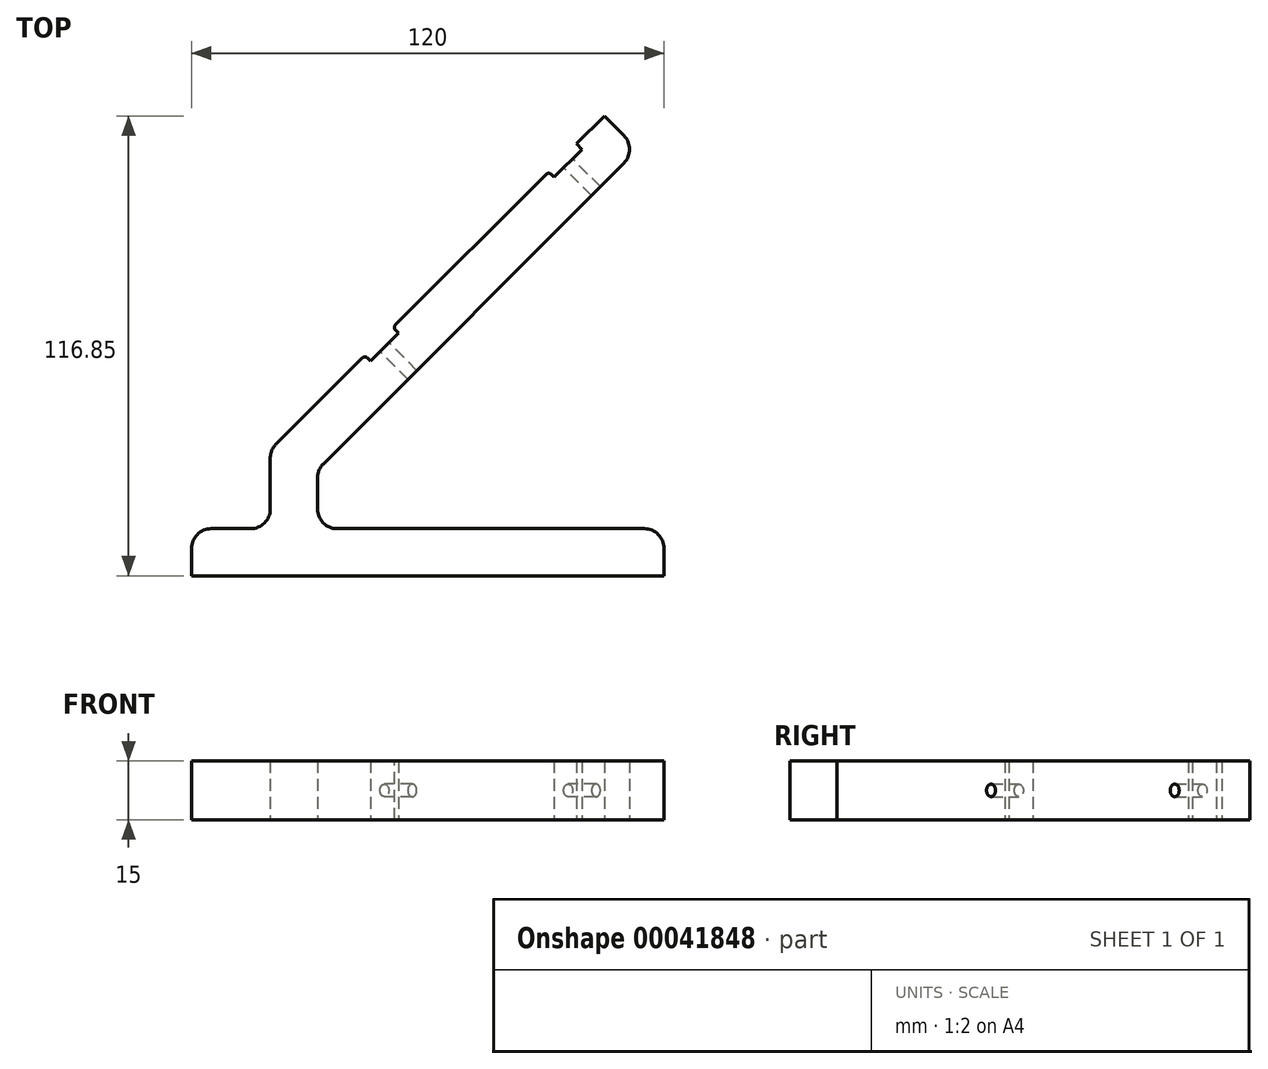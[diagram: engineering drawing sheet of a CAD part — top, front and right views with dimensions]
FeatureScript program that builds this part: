
annotation { "Feature Type Name" : "Feature", "Feature Type Description" : "" }
export const myFeature = defineFeature(function(context is Context, id is Id, definition is map)
    precondition{}
    {
        {
            var Q0;
            Q0=qCreatedBy(makeId("Top.planeOp"),FACE);
            var sketch = newSketch(context, id + "F0", { "sketchPlane" : qUnion([Q0])});
            skLineSegment(sketch, "E0.bottom", {"start": v(60, -6) * mm, "end": v(-60, -6) * mm});
            skLineSegment(sketch, "E0.top", {"start": v(60, 6) * mm, "end": v(-60, 6) * mm});
            skLineSegment(sketch, "E0.left", {"start": v(60, -6) * mm, "end": v(60, 6) * mm});
            skLineSegment(sketch, "E0.right", {"start": v(-60, -6) * mm, "end": v(-60, 6) * mm});
            skPoint(sketch, "E0.middle", {"position": v(0, 0) * mm});
            skLineSegment(sketch, "E1", {"start": v(-40, 26) * mm, "end": v(44.85, 110.85) * mm});
            skLineSegment(sketch, "E2", {"start": v(44.85, 110.85) * mm, "end": v(53.34, 102.37) * mm});
            skLineSegment(sketch, "E3", {"start": v(53.34, 102.37) * mm, "end": v(-28, 21.03) * mm});
            skLineSegment(sketch, "E4", {"start": v(-40, 26) * mm, "end": v(-40, 6) * mm});
            skLineSegment(sketch, "E5", {"start": v(-28, 21.03) * mm, "end": v(-28, 6) * mm});
            skSolve(sketch);
        }
        {
            var Q0;
            {var subQ0=sQuery(id+"F0.wireOp",EDGE,"E1");Q0=makeQuery(id+"F0.imprint","IMPRINT",FACE,{"disambiguationData":[TD([[makeQuery(id+"F0.imprint","IMPRINT",EDGE,{"derivedFrom":subQ0}),-1.0]])]});}
            var Q1;
            Q1=makeQuery(id+"F0.imprint","IMPRINT",FACE,{"disambiguationData":[TD([[makeQuery(id+"F0.imprint","IMPRINT",EDGE,{"derivedFrom":sQuery(id+"F0.wireOp",EDGE,"E0.bottom")}),-1.0]])]});
            extrude(context, id + "F1", {"entities" : qUnion([Q0, Q1]), "depth" : 15 * mm});
        }
        {
            var Q0;
            Q0=makeQuery(id+"F1.opExtrude","SWEPT_EDGE",EDGE,{"disambiguationData":[OSD([sQuery(id+"F0.wireOp",EDGE,"E0.top"),sQuery(id+"F0.wireOp",EDGE,"E3")])]});
            var Q1;
            Q1=makeQuery(id+"F1.opExtrude","SWEPT_EDGE",EDGE,{"disambiguationData":[OSD([sQuery(id+"F0.wireOp",EDGE,"E0.top"),sQuery(id+"F0.wireOp",EDGE,"E0.right")])]});
            var Q2;
            Q2=makeQuery(id+"F1.opExtrude","SWEPT_EDGE",EDGE,{"disambiguationData":[OSD([sQuery(id+"F0.wireOp",EDGE,"E0.top"),sQuery(id+"F0.wireOp",EDGE,"E0.left")])]});
            var Q3;
            Q3=makeQuery(id+"F1.opExtrude","SWEPT_EDGE",EDGE,{"disambiguationData":[OSD([sQuery(id+"F0.wireOp",EDGE,"E2"),sQuery(id+"F0.wireOp",EDGE,"E3")])]});
            var Q4;
            Q4=makeQuery(id+"F1.opExtrude","SWEPT_EDGE",EDGE,{"disambiguationData":[OSD([sQuery(id+"F0.wireOp",EDGE,"E1"),sQuery(id+"F0.wireOp",EDGE,"E4")])]});
            fillet(context, id + "F2", {"entities" : qUnion([Q0, Q1, Q2, Q3, Q4]), "radius" : 5 * mm, "tangentPropagation" : true, "allowEdgeOverflow" : false});
        }
        {
            var Q0;
            Q0=makeQuery(id+"F1.opExtrude","SWEPT_FACE",FACE,{"disambiguationData":[OSD([sQuery(id+"F0.wireOp",EDGE,"E1")])]});
            var sketch = newSketch(context, id + "F3", { "sketchPlane" : qUnion([Q0])});
            skPoint(sketch, "E6", {"position": v(-95.1, 7.5) * mm});
            skPoint(sketch, "E6.positionSnap0", {"position": v(-110.1, 7.5) * mm});
            skPoint(sketch, "E7", {"position": v(-29.1, 7.5) * mm});
            skLineSegment(sketch, "E8.bottom", {"start": v(-90.1, 15) * mm, "end": v(-100.1, 15) * mm});
            skLineSegment(sketch, "E8.top", {"start": v(-90.1, 0) * mm, "end": v(-100.1, 0) * mm});
            skLineSegment(sketch, "E8.left", {"start": v(-90.1, 15) * mm, "end": v(-90.1, 0) * mm});
            skLineSegment(sketch, "E8.right", {"start": v(-100.1, 15) * mm, "end": v(-100.1, 0) * mm});
            skLineSegment(sketch, "E9.bottom", {"start": v(-24.1, 15) * mm, "end": v(-34.1, 15) * mm});
            skLineSegment(sketch, "E9.top", {"start": v(-24.1, 0) * mm, "end": v(-34.1, 0) * mm});
            skLineSegment(sketch, "E9.left", {"start": v(-24.1, 15) * mm, "end": v(-24.1, 0) * mm});
            skLineSegment(sketch, "E9.right", {"start": v(-34.1, 15) * mm, "end": v(-34.1, 0) * mm});
            skSolve(sketch);
        }
        {
            var Q0;
            Q0=makeQuery(id+"F3.imprint","IMPRINT",FACE,{"disambiguationData":[TD([[makeQuery(id+"F3.imprint","IMPRINT",EDGE,{"derivedFrom":sQuery(id+"F3.wireOp",EDGE,"E8.bottom")}),1.0]])]});
            var Q1;
            Q1=makeQuery(id+"F3.imprint","IMPRINT",FACE,{"disambiguationData":[TD([[makeQuery(id+"F3.imprint","IMPRINT",EDGE,{"derivedFrom":sQuery(id+"F3.wireOp",EDGE,"E9.bottom")}),1.0]])]});
            extrude(context, id + "F4", {"entities" : qUnion([Q0, Q1]), "operationType" : NewBodyOperationType.REMOVE, "oppositeDirection" : true, "depth" : 2 * mm});
        }
        {
            var Q0;
            Q0=sQuery(id+"F3.wireOp",VERTEX,"E6");
            var Q1;
            Q1=sQuery(id+"F3.wireOp",VERTEX,"E7");
            var Q2;
            Q2=makeQuery(id+"F1.opExtrude","SWEPT_BODY",BODY,{"disambiguationData":[OSD([sQuery(id+"F0.wireOp",EDGE,"E0.bottom"),sQuery(id+"F0.wireOp",EDGE,"E0.top"),sQuery(id+"F0.wireOp",EDGE,"E0.left"),sQuery(id+"F0.wireOp",EDGE,"E0.right"),sQuery(id+"F0.wireOp",EDGE,"E1"),sQuery(id+"F0.wireOp",EDGE,"E2"),sQuery(id+"F0.wireOp",EDGE,"E3")])]});
            hole(context, id + "F5", {"style" : HoleStyle.SIMPLE, "endStyle" : HoleEndStyle.BLIND, "holeDiameter" : 3.2 * mm, "holeDepth" : 25 * mm, "startFromSketch" : true, "locations" : qUnion([Q0, Q1]), "scope" : qUnion([Q2])});
        }
        {
            var Q0;
            Q0=makeQuery(id+"F4.boolean.opBoolean","COPY",EDGE,{"derivedFrom":makeQuery(id+"F4.opExtrude","CAP_EDGE",EDGE,{"disambiguationData":[OSD([sQuery(id+"F3.wireOp",EDGE,"E8.right")])],"isStart":true})});
            var Q1;
            Q1=makeQuery(id+"F4.boolean.opBoolean","COPY",EDGE,{"derivedFrom":makeQuery(id+"F4.opExtrude","CAP_EDGE",EDGE,{"disambiguationData":[OSD([sQuery(id+"F3.wireOp",EDGE,"E8.left")])],"isStart":true})});
            var Q2;
            Q2=makeQuery(id+"F4.boolean.opBoolean","COPY",EDGE,{"derivedFrom":makeQuery(id+"F4.opExtrude","CAP_EDGE",EDGE,{"disambiguationData":[OSD([sQuery(id+"F3.wireOp",EDGE,"E9.right")])],"isStart":true})});
            var Q3;
            Q3=makeQuery(id+"F4.boolean.opBoolean","COPY",EDGE,{"derivedFrom":makeQuery(id+"F4.opExtrude","CAP_EDGE",EDGE,{"disambiguationData":[OSD([sQuery(id+"F3.wireOp",EDGE,"E9.left")])],"isStart":true})});
            fillet(context, id + "F6", {"entities" : qUnion([Q0, Q1, Q2, Q3]), "radius" : 1 * mm, "tangentPropagation" : true, "allowEdgeOverflow" : false});
        }
    });
